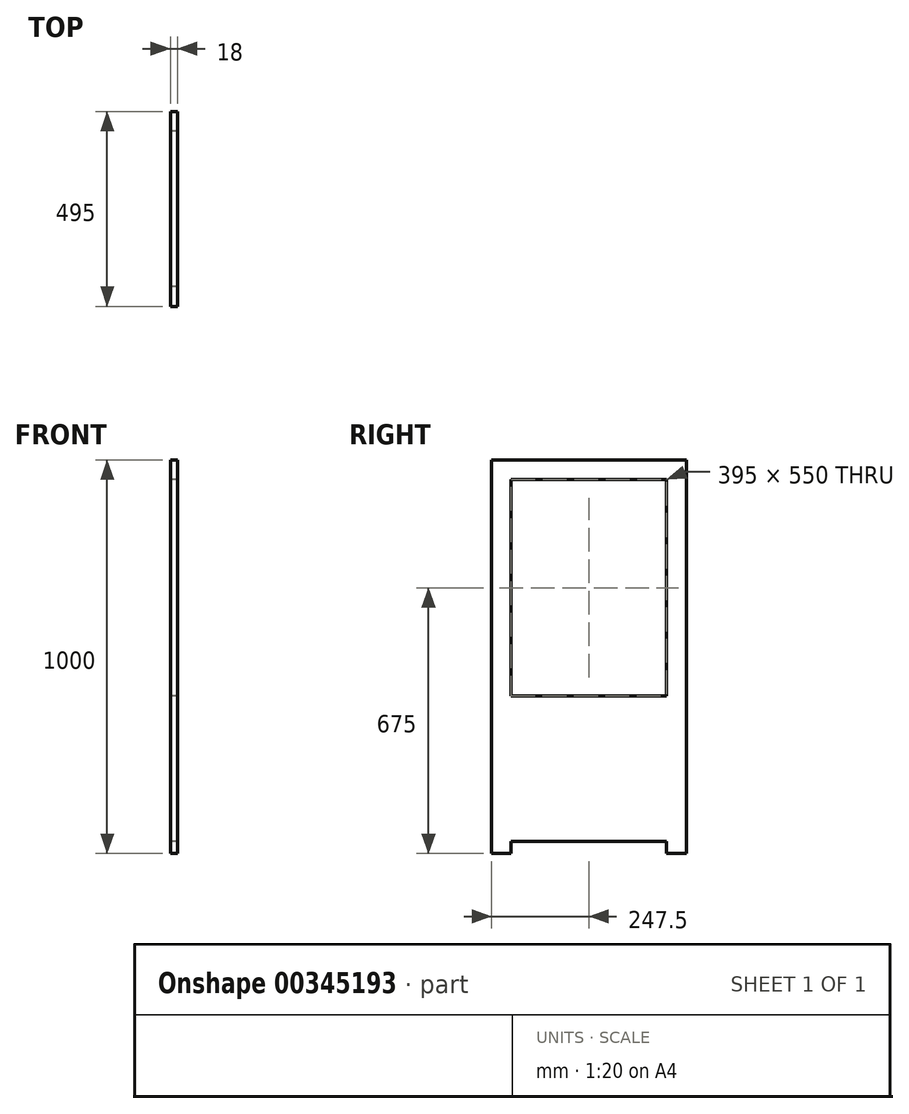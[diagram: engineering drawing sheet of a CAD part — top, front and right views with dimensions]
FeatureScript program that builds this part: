
annotation { "Feature Type Name" : "Feature", "Feature Type Description" : "" }
export const myFeature = defineFeature(function(context is Context, id is Id, definition is map)
    precondition{}
    {
        {
            var Q0;
            Q0=qCreatedBy(makeId("Right.planeOp"),FACE);
            var sketch = newSketch(context, id + "F0", { "sketchPlane" : qUnion([Q0])});
            skLineSegment(sketch, "E0", {"start": v(0, 0) * mm, "end": v(0, 1000) * mm});
            skLineSegment(sketch, "E1", {"start": v(0, 1000) * mm, "end": v(495, 1000) * mm});
            skLineSegment(sketch, "E2", {"start": v(495, 1000) * mm, "end": v(495, 0) * mm});
            skLineSegment(sketch, "E3", {"start": v(495, 0) * mm, "end": v(445, 0) * mm});
            skLineSegment(sketch, "E4", {"start": v(50, 950) * mm, "end": v(50, 400) * mm});
            skLineSegment(sketch, "E5", {"start": v(50, 400) * mm, "end": v(445, 400) * mm});
            skLineSegment(sketch, "E6", {"start": v(445, 400) * mm, "end": v(445, 950) * mm});
            skLineSegment(sketch, "E7", {"start": v(445, 950) * mm, "end": v(50, 950) * mm});
            skLineSegment(sketch, "E8", {"start": v(50, 0) * mm, "end": v(50, 30) * mm});
            skLineSegment(sketch, "E9", {"start": v(50, 30) * mm, "end": v(445, 30) * mm});
            skLineSegment(sketch, "E10", {"start": v(445, 30) * mm, "end": v(445, 0) * mm});
            skLineSegment(sketch, "E11.trimOffspring", {"start": v(50, 0) * mm, "end": v(0, 0) * mm});
            skSolve(sketch);
        }
        {
            var Q0;
            Q0 = qSketchRegion(id + "F0", true);
            extrude(context, id + "F1", {"entities" : qUnion([Q0]), "depth" : 18 * mm});
        }
    });
